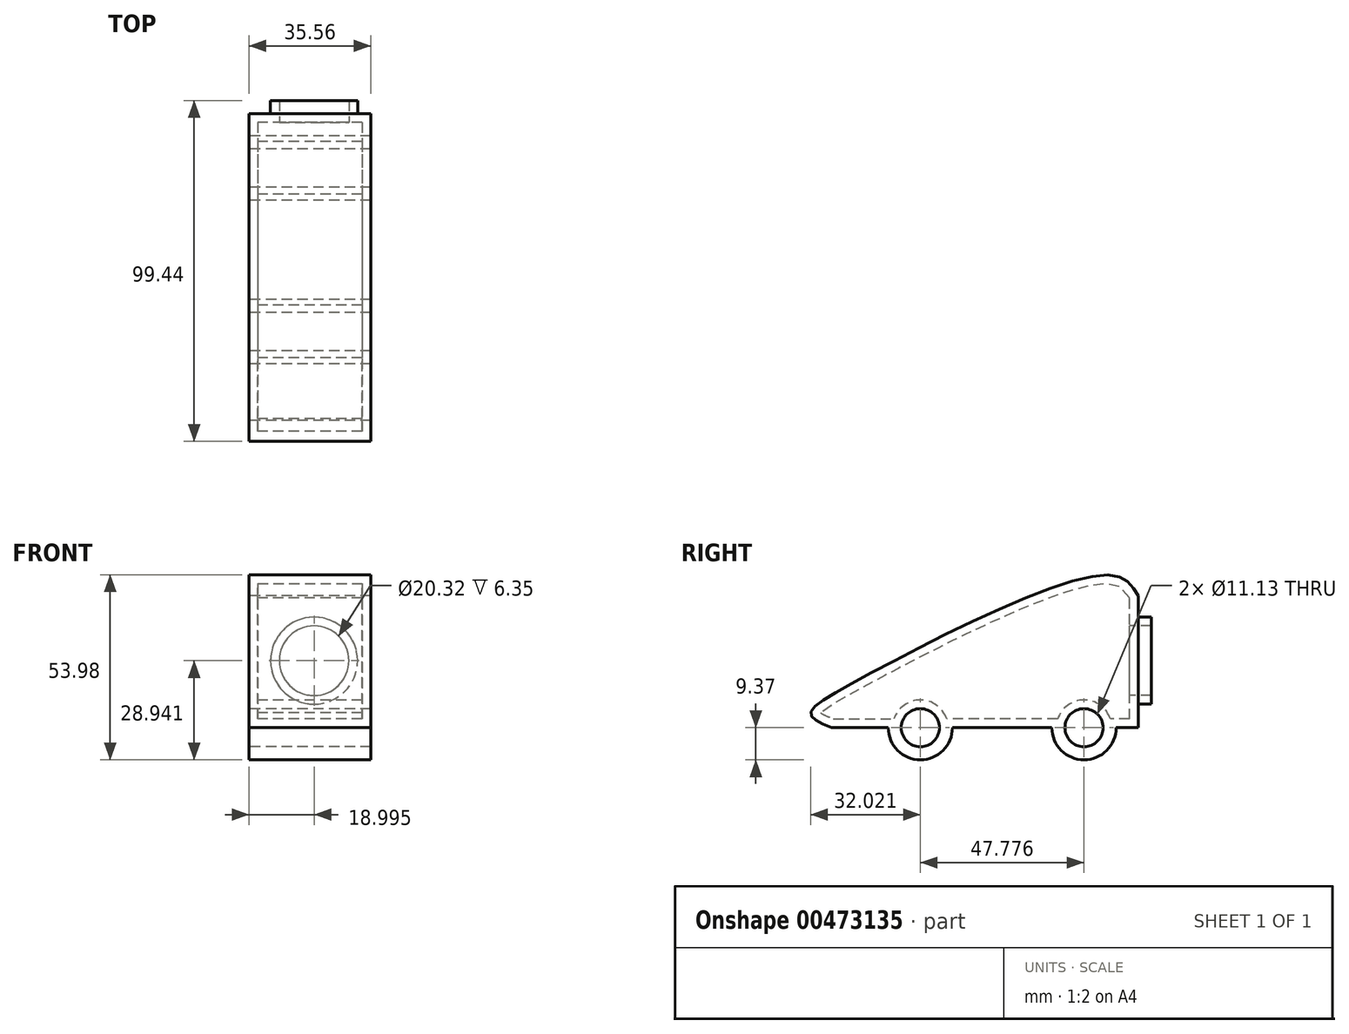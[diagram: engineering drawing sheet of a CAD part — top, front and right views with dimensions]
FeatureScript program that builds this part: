
annotation { "Feature Type Name" : "Feature", "Feature Type Description" : "" }
export const myFeature = defineFeature(function(context is Context, id is Id, definition is map)
    precondition{}
    {
        {
            var Q0;
            Q0=qCreatedBy(makeId("Right.planeOp"),FACE);
            var sketch = newSketch(context, id + "F0", { "sketchPlane" : qUnion([Q0])});
            skLineSegment(sketch, "E0", {"start": v(71.38, 0) * mm, "end": v(71.38, 38.57) * mm});
            skFitSpline(sketch, "E1", {"points": [v(71.38, 38.57) * mm, v(62.45, 44.6) * mm, v(-12.66, 12.66) * mm, v(-24.18, 3.74) * mm, v(-18.13, 0) * mm], "startDerivative": vector(-30.9, 51.17) * mm, "endDerivative": vector(59.02, -24.78) * mm});
            skCircle(sketch, "E2", {"center": v(55.55, 0) * mm, "radius": 9.37 * mm});
            skCircle(sketch, "E3", {"center": v(7.77, 0) * mm, "radius": 9.37 * mm});
            skLineSegment(sketch, "E4", {"start": v(71.38, 0) * mm, "end": v(64.92, 0) * mm});
            skLineSegment(sketch, "E5", {"start": v(64.92, 0) * mm, "end": v(71.38, 0) * mm});
            skLineSegment(sketch, "E6", {"start": v(46.17, 0) * mm, "end": v(17.14, 0) * mm});
            skPoint(sketch, "E6.startSnap0", {"position": v(68.15, 0) * mm});
            skLineSegment(sketch, "E7", {"start": v(17.14, 0) * mm, "end": v(46.17, 0) * mm});
            skLineSegment(sketch, "E8", {"start": v(-18.13, 0) * mm, "end": v(-1.6, 0) * mm});
            skLineSegment(sketch, "E9", {"start": v(-1.6, 0) * mm, "end": v(-18.13, 0) * mm});
            skCircle(sketch, "E10", {"center": v(7.77, 0) * mm, "radius": 5.56 * mm});
            skCircle(sketch, "E11", {"center": v(55.55, 0) * mm, "radius": 5.56 * mm});
            skSolve(sketch);
        }
        {
            var Q0;
            Q0 = qSketchRegion(id + "F0", true);
            extrude(context, id + "F1", {"entities" : qUnion([Q0]), "depth" : 35.56 * mm});
        }
        {
            var Q0;
            Q0=makeQuery(id+"F1.opExtrude","SWEPT_FACE",FACE,{"disambiguationData":[OSD([sQuery(id+"F0.wireOp",EDGE,"E0")])]});
            var sketch = newSketch(context, id + "F2", { "sketchPlane" : qUnion([Q0])});
            skCircle(sketch, "E12", {"center": v(-19, 19.57) * mm, "radius": 12.7 * mm});
            skSolve(sketch);
        }
        {
            var Q0;
            Q0 = qSketchRegion(id + "F2", true);
            extrude(context, id + "F3", {"entities" : qUnion([Q0]), "operationType" : NewBodyOperationType.ADD, "depth" : 3.8 * mm});
        }
        {
            var Q0;
            Q0=makeQuery(id+"F3.opExtrude","CAP_FACE",FACE,{"disambiguationData":[OSD([sQuery(id+"F2.wireOp",EDGE,"E12")])],"isStart":false});
            shell(context, id + "F4", {"entities" : qUnion([Q0]), "thickness" : 2.54 * mm});
        }
    });
